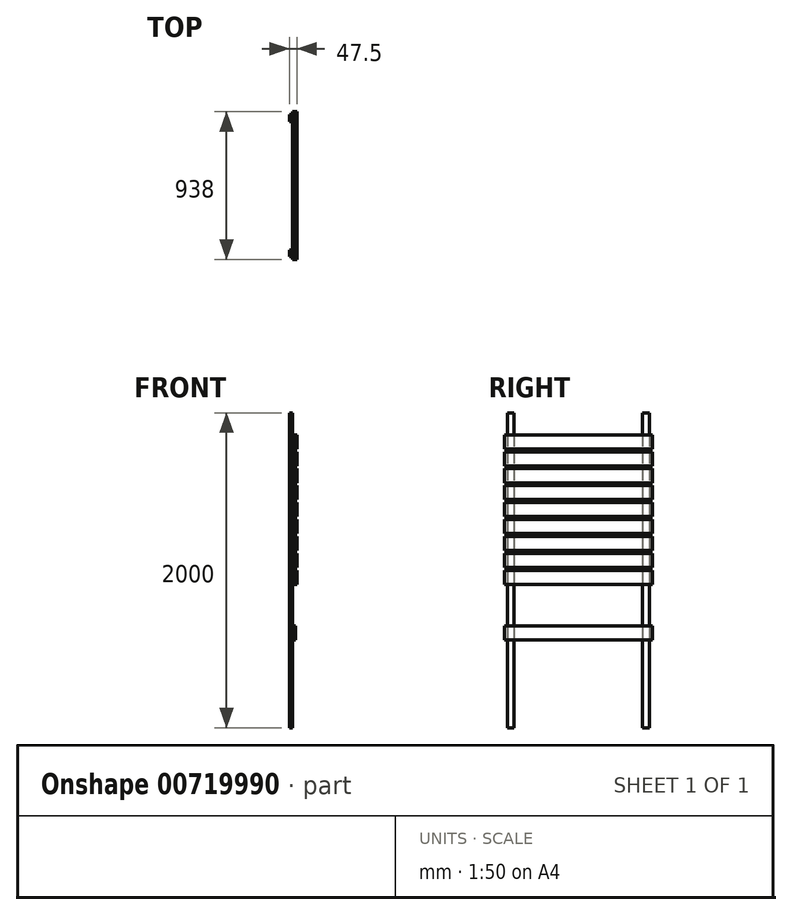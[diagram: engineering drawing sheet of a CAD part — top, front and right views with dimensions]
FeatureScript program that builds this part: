
annotation { "Feature Type Name" : "Feature", "Feature Type Description" : "" }
export const myFeature = defineFeature(function(context is Context, id is Id, definition is map)
    precondition{}
    {
        {
            var Q0;
            Q0=qCreatedBy(makeId("Top.planeOp"),FACE);
            var sketch = newSketch(context, id + "F0", { "sketchPlane" : qUnion([Q0])});
            skLineSegment(sketch, "E0.bottom", {"start": v(9.5, -469) * mm, "end": v(-9.5, -469) * mm});
            skLineSegment(sketch, "E0.top", {"start": v(9.5, 469) * mm, "end": v(-9.5, 469) * mm});
            skLineSegment(sketch, "E0.left", {"start": v(9.5, -469) * mm, "end": v(9.5, 469) * mm});
            skLineSegment(sketch, "E0.right", {"start": v(-9.5, -469) * mm, "end": v(-9.5, 469) * mm});
            skPoint(sketch, "E0.middle", {"position": v(0, 0) * mm});
            skLineSegment(sketch, "E1.top", {"start": v(-9.5, -450) * mm, "end": v(-28.5, -450) * mm});
            skLineSegment(sketch, "E1.left", {"start": v(-9.5, -469) * mm, "end": v(-9.5, -450) * mm});
            skLineSegment(sketch, "E2.top", {"start": v(-9.5, -408) * mm, "end": v(-28.5, -408) * mm});
            skLineSegment(sketch, "E2.left", {"start": v(-9.5, -450) * mm, "end": v(-9.5, -408) * mm});
            skLineSegment(sketch, "E2.right", {"start": v(-28.5, -450) * mm, "end": v(-28.5, -408) * mm});
            skLineSegment(sketch, "E3.top", {"start": v(-9.5, 450) * mm, "end": v(-28.5, 450) * mm});
            skLineSegment(sketch, "E3.left", {"start": v(-9.5, 469) * mm, "end": v(-9.5, 450) * mm});
            skLineSegment(sketch, "E4.top", {"start": v(-9.5, 408) * mm, "end": v(-28.5, 408) * mm});
            skLineSegment(sketch, "E4.left", {"start": v(-9.5, 450) * mm, "end": v(-9.5, 408) * mm});
            skLineSegment(sketch, "E4.right", {"start": v(-28.5, 450) * mm, "end": v(-28.5, 408) * mm});
            skSolve(sketch);
        }
        {
            var Q0;
            Q0 = qSketchRegion(id + "F0", true);
            extrude(context, id + "F1", {"entities" : qUnion([Q0]), "depth" : 89 * mm, "offsetDistance" : 25 * mm});
        }
        {
            var Q0;
            Q0=makeQuery(id+"F0.imprint","IMPRINT",FACE,{"disambiguationData":[TD([[makeQuery(id+"F0.imprint","IMPRINT",EDGE,{"derivedFrom":sQuery(id+"F0.wireOp",EDGE,"E1.top")}),-1.0]])]});
            var Q1;
            Q1=makeQuery(id+"F0.imprint","IMPRINT",FACE,{"disambiguationData":[TD([[makeQuery(id+"F0.imprint","IMPRINT",EDGE,{"derivedFrom":sQuery(id+"F0.wireOp",EDGE,"E3.top")}),1.0]])]});
            extrude(context, id + "F2", {"entities" : qUnion([Q0, Q1]), "operationType" : NewBodyOperationType.ADD, "oppositeDirection" : true, "depth" : 557 * mm, "offsetDistance" : 25 * mm});
        }
        {
            var Q0;
            Q0=makeQuery(id+"F2.opExtrude","CAP_FACE",FACE,{"disambiguationData":[OSD([sQuery(id+"F0.wireOp",EDGE,"E3.top"),sQuery(id+"F0.wireOp",EDGE,"E4.top"),sQuery(id+"F0.wireOp",EDGE,"E4.left"),sQuery(id+"F0.wireOp",EDGE,"E4.right")])],"isStart":false});
            var Q1;
            Q1=makeQuery(id+"F2.opExtrude","CAP_FACE",FACE,{"disambiguationData":[OSD([sQuery(id+"F0.wireOp",EDGE,"E1.top"),sQuery(id+"F0.wireOp",EDGE,"E2.top"),sQuery(id+"F0.wireOp",EDGE,"E2.left"),sQuery(id+"F0.wireOp",EDGE,"E2.right")])],"isStart":false});
            var Q2;
            Q2 = qSketchRegion(id + "F4", true);
            extrude(context, id + "F3", {"entities" : qUnion([Q0, Q1, Q2]), "operationType" : NewBodyOperationType.ADD, "oppositeDirection" : true, "depth" : 2000 * mm, "offsetDistance" : 25 * mm});
        }
        {
            var Q0;
            Q0=qCreatedBy(makeId("Right.planeOp"),FACE);
            var sketch = newSketch(context, id + "F4", { "sketchPlane" : qUnion([Q0])});
            skLineSegment(sketch, "E5.bottom", {"start": v(0, 658.7) * mm, "end": v(469, 658.7) * mm});
            skLineSegment(sketch, "E5.top", {"start": v(0, 569.7) * mm, "end": v(469, 569.7) * mm});
            skLineSegment(sketch, "E5.left", {"start": v(0, 658.7) * mm, "end": v(0, 569.7) * mm});
            skLineSegment(sketch, "E5.right", {"start": v(469, 658.7) * mm, "end": v(469, 569.7) * mm});
            skLineSegment(sketch, "E6.bottom", {"start": v(0, 658.7) * mm, "end": v(-469, 658.7) * mm});
            skLineSegment(sketch, "E6.top", {"start": v(0, 569.7) * mm, "end": v(-469, 569.7) * mm});
            skLineSegment(sketch, "E6.right", {"start": v(-469, 658.7) * mm, "end": v(-469, 569.7) * mm});
            skLineSegment(sketch, "E7.bottom", {"start": v(0, 569.7) * mm, "end": v(51.52, 569.7) * mm});
            skLineSegment(sketch, "E7.top", {"start": v(0, 551.2) * mm, "end": v(51.52, 551.2) * mm});
            skLineSegment(sketch, "E7.left", {"start": v(0, 569.7) * mm, "end": v(0, 551.2) * mm});
            skLineSegment(sketch, "E8.bottom", {"start": v(0, 551.2) * mm, "end": v(469, 551.2) * mm});
            skLineSegment(sketch, "E8.top", {"start": v(0, 462.2) * mm, "end": v(469, 462.2) * mm});
            skLineSegment(sketch, "E8.left", {"start": v(0, 551.2) * mm, "end": v(0, 462.2) * mm});
            skLineSegment(sketch, "E8.right", {"start": v(469, 551.2) * mm, "end": v(469, 462.2) * mm});
            skLineSegment(sketch, "E9.bottom", {"start": v(0, 551.2) * mm, "end": v(-469, 551.2) * mm});
            skLineSegment(sketch, "E9.top", {"start": v(0, 462.2) * mm, "end": v(-469, 462.2) * mm});
            skLineSegment(sketch, "E9.right", {"start": v(-469, 551.2) * mm, "end": v(-469, 462.2) * mm});
            skLineSegment(sketch, "E10.bottom", {"start": v(0, 462.2) * mm, "end": v(64.74, 462.2) * mm});
            skLineSegment(sketch, "E10.top", {"start": v(0, 443.7) * mm, "end": v(64.74, 443.7) * mm});
            skLineSegment(sketch, "E10.left", {"start": v(0, 462.2) * mm, "end": v(0, 443.7) * mm});
            skLineSegment(sketch, "E11.bottom", {"start": v(0, 443.7) * mm, "end": v(469, 443.7) * mm});
            skLineSegment(sketch, "E11.top", {"start": v(0, 354.7) * mm, "end": v(469, 354.7) * mm});
            skLineSegment(sketch, "E11.left", {"start": v(0, 443.7) * mm, "end": v(0, 354.7) * mm});
            skLineSegment(sketch, "E11.right", {"start": v(469, 443.7) * mm, "end": v(469, 354.7) * mm});
            skLineSegment(sketch, "E12.bottom", {"start": v(0, 443.7) * mm, "end": v(-469, 443.7) * mm});
            skLineSegment(sketch, "E12.top", {"start": v(0, 354.7) * mm, "end": v(-469, 354.7) * mm});
            skLineSegment(sketch, "E12.right", {"start": v(-469, 443.7) * mm, "end": v(-469, 354.7) * mm});
            skLineSegment(sketch, "E13.bottom", {"start": v(0, 658.7) * mm, "end": v(59.09, 658.7) * mm});
            skLineSegment(sketch, "E13.top", {"start": v(0, 677.2) * mm, "end": v(59.09, 677.2) * mm});
            skLineSegment(sketch, "E13.left", {"start": v(0, 658.7) * mm, "end": v(0, 677.2) * mm});
            skLineSegment(sketch, "E14.bottom", {"start": v(0, 677.2) * mm, "end": v(469, 677.2) * mm});
            skLineSegment(sketch, "E14.top", {"start": v(0, 766.2) * mm, "end": v(469, 766.2) * mm});
            skLineSegment(sketch, "E14.left", {"start": v(0, 677.2) * mm, "end": v(0, 766.2) * mm});
            skLineSegment(sketch, "E14.right", {"start": v(469, 677.2) * mm, "end": v(469, 766.2) * mm});
            skLineSegment(sketch, "E15.bottom", {"start": v(0, 677.2) * mm, "end": v(-469, 677.2) * mm});
            skLineSegment(sketch, "E15.top", {"start": v(0, 766.2) * mm, "end": v(-469, 766.2) * mm});
            skLineSegment(sketch, "E15.right", {"start": v(-469, 677.2) * mm, "end": v(-469, 766.2) * mm});
            skLineSegment(sketch, "E16.bottom", {"start": v(0, 766.2) * mm, "end": v(90.52, 766.2) * mm});
            skLineSegment(sketch, "E16.top", {"start": v(0, 784.7) * mm, "end": v(90.52, 784.7) * mm});
            skLineSegment(sketch, "E16.left", {"start": v(0, 766.2) * mm, "end": v(0, 784.7) * mm});
            skLineSegment(sketch, "E17.bottom", {"start": v(0, 784.7) * mm, "end": v(469, 784.7) * mm});
            skLineSegment(sketch, "E17.top", {"start": v(0, 873.7) * mm, "end": v(469, 873.7) * mm});
            skLineSegment(sketch, "E17.left", {"start": v(0, 784.7) * mm, "end": v(0, 873.7) * mm});
            skLineSegment(sketch, "E17.right", {"start": v(469, 784.7) * mm, "end": v(469, 873.7) * mm});
            skLineSegment(sketch, "E18.bottom", {"start": v(0, 784.7) * mm, "end": v(-469, 784.7) * mm});
            skLineSegment(sketch, "E18.top", {"start": v(0, 873.7) * mm, "end": v(-469, 873.7) * mm});
            skLineSegment(sketch, "E18.right", {"start": v(-469, 784.7) * mm, "end": v(-469, 873.7) * mm});
            skLineSegment(sketch, "E19.bottom", {"start": v(0, 873.7) * mm, "end": v(57.99, 873.7) * mm});
            skLineSegment(sketch, "E19.top", {"start": v(0, 892.2) * mm, "end": v(57.99, 892.2) * mm});
            skLineSegment(sketch, "E19.left", {"start": v(0, 873.7) * mm, "end": v(0, 892.2) * mm});
            skLineSegment(sketch, "E20.bottom", {"start": v(0, 892.2) * mm, "end": v(469, 892.2) * mm});
            skLineSegment(sketch, "E20.top", {"start": v(0, 981.2) * mm, "end": v(469, 981.2) * mm});
            skLineSegment(sketch, "E20.left", {"start": v(0, 892.2) * mm, "end": v(0, 981.2) * mm});
            skLineSegment(sketch, "E20.right", {"start": v(469, 892.2) * mm, "end": v(469, 981.2) * mm});
            skLineSegment(sketch, "E21.bottom", {"start": v(0, 892.2) * mm, "end": v(-469, 892.2) * mm});
            skLineSegment(sketch, "E21.top", {"start": v(0, 981.2) * mm, "end": v(-469, 981.2) * mm});
            skLineSegment(sketch, "E21.right", {"start": v(-469, 892.2) * mm, "end": v(-469, 981.2) * mm});
            skLineSegment(sketch, "E22.bottom", {"start": v(0, 981.2) * mm, "end": v(44.3, 981.2) * mm});
            skLineSegment(sketch, "E22.top", {"start": v(0, 999.7) * mm, "end": v(44.3, 999.7) * mm});
            skLineSegment(sketch, "E22.left", {"start": v(0, 981.2) * mm, "end": v(0, 999.7) * mm});
            skLineSegment(sketch, "E23.bottom", {"start": v(0, 999.7) * mm, "end": v(469, 999.7) * mm});
            skLineSegment(sketch, "E23.top", {"start": v(0, 1088.7) * mm, "end": v(469, 1088.7) * mm});
            skLineSegment(sketch, "E23.left", {"start": v(0, 999.7) * mm, "end": v(0, 1088.7) * mm});
            skLineSegment(sketch, "E23.right", {"start": v(469, 999.7) * mm, "end": v(469, 1088.7) * mm});
            skLineSegment(sketch, "E24.bottom", {"start": v(0, 999.7) * mm, "end": v(-469, 999.7) * mm});
            skLineSegment(sketch, "E24.top", {"start": v(0, 1088.7) * mm, "end": v(-469, 1088.7) * mm});
            skLineSegment(sketch, "E24.right", {"start": v(-469, 999.7) * mm, "end": v(-469, 1088.7) * mm});
            skLineSegment(sketch, "E25.bottom", {"start": v(0, 1088.7) * mm, "end": v(34.16, 1088.7) * mm});
            skLineSegment(sketch, "E25.top", {"start": v(0, 1107.2) * mm, "end": v(34.16, 1107.2) * mm});
            skLineSegment(sketch, "E25.left", {"start": v(0, 1088.7) * mm, "end": v(0, 1107.2) * mm});
            skLineSegment(sketch, "E26.bottom", {"start": v(0, 1107.2) * mm, "end": v(469, 1107.2) * mm});
            skLineSegment(sketch, "E26.top", {"start": v(0, 1196.2) * mm, "end": v(469, 1196.2) * mm});
            skLineSegment(sketch, "E26.left", {"start": v(0, 1107.2) * mm, "end": v(0, 1196.2) * mm});
            skLineSegment(sketch, "E26.right", {"start": v(469, 1107.2) * mm, "end": v(469, 1196.2) * mm});
            skLineSegment(sketch, "E27.bottom", {"start": v(0, 1107.2) * mm, "end": v(-469, 1107.2) * mm});
            skLineSegment(sketch, "E27.top", {"start": v(0, 1196.2) * mm, "end": v(-469, 1196.2) * mm});
            skLineSegment(sketch, "E27.right", {"start": v(-469, 1107.2) * mm, "end": v(-469, 1196.2) * mm});
            skLineSegment(sketch, "E28.bottom", {"start": v(0, 1196.2) * mm, "end": v(46.12, 1196.2) * mm});
            skLineSegment(sketch, "E28.top", {"start": v(0, 1214.7) * mm, "end": v(46.12, 1214.7) * mm});
            skLineSegment(sketch, "E28.left", {"start": v(0, 1196.2) * mm, "end": v(0, 1214.7) * mm});
            skLineSegment(sketch, "E29.bottom", {"start": v(0, 1214.7) * mm, "end": v(469, 1214.7) * mm});
            skLineSegment(sketch, "E29.top", {"start": v(0, 1303.7) * mm, "end": v(469, 1303.7) * mm});
            skLineSegment(sketch, "E29.left", {"start": v(0, 1214.7) * mm, "end": v(0, 1303.7) * mm});
            skLineSegment(sketch, "E29.right", {"start": v(469, 1214.7) * mm, "end": v(469, 1303.7) * mm});
            skLineSegment(sketch, "E30.bottom", {"start": v(0, 1214.7) * mm, "end": v(-469, 1214.7) * mm});
            skLineSegment(sketch, "E30.top", {"start": v(0, 1303.7) * mm, "end": v(-469, 1303.7) * mm});
            skLineSegment(sketch, "E30.right", {"start": v(-469, 1214.7) * mm, "end": v(-469, 1303.7) * mm});
            skSolve(sketch);
        }
        {
            var Q0;
            Q0 = qSketchRegion(id + "F4", true);
            extrude(context, id + "F5", {"entities" : qUnion([Q0]), "depth" : 19 * mm, "offsetDistance" : 25 * mm});
        }
    });
